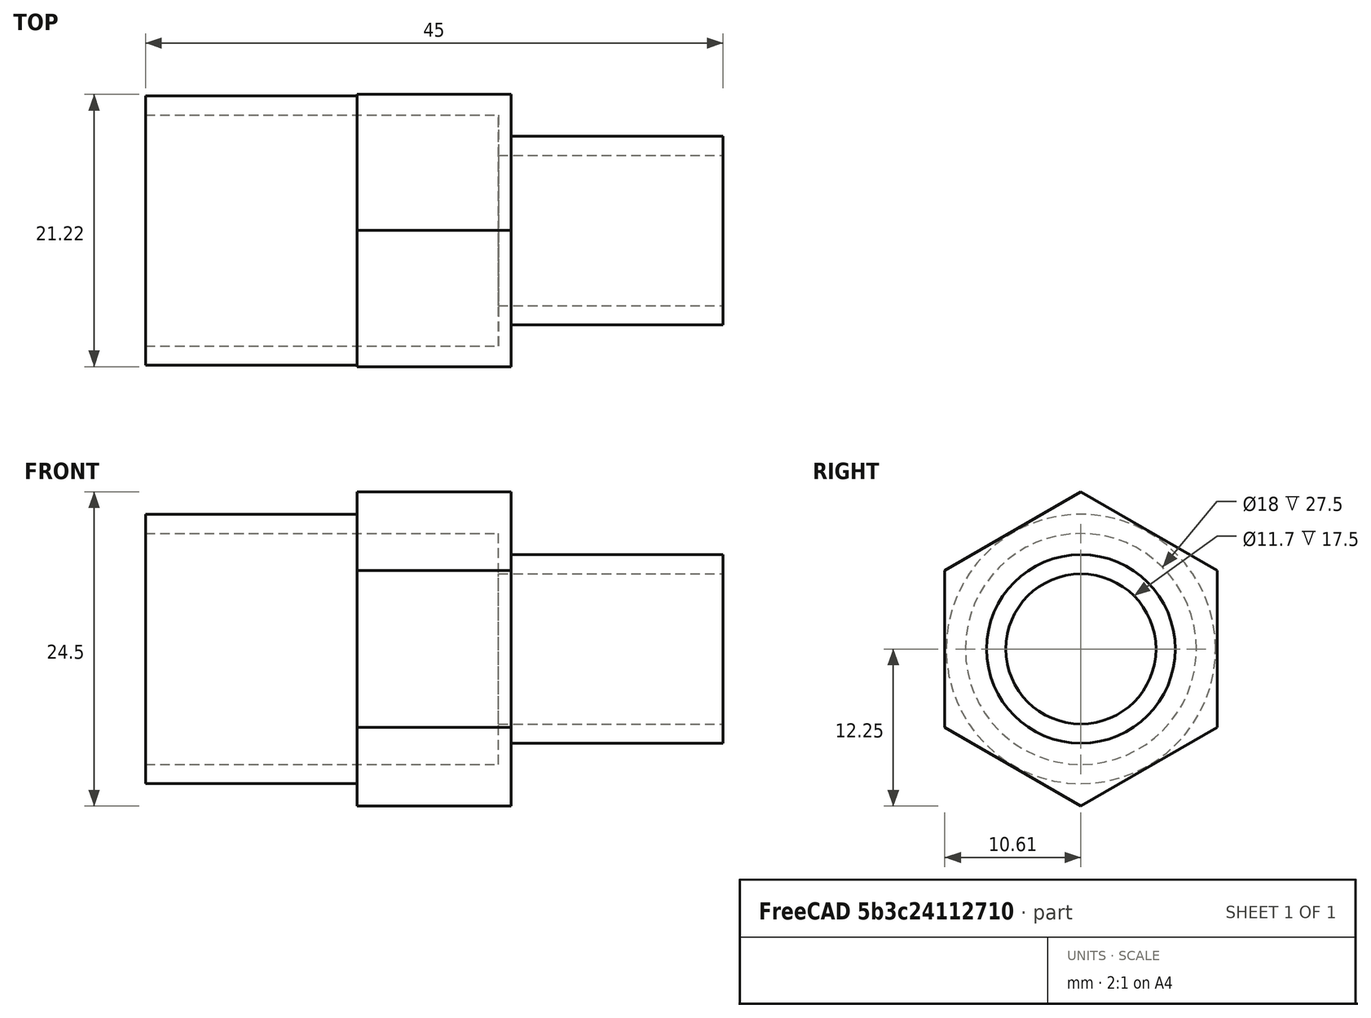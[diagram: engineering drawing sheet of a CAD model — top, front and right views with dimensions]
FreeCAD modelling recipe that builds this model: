
FCSTD DOCUMENT  (FreeCAD 0.16R6706 (Git))
Label: 1_2_to_3_4_NPT_HexNipple
License: All rights reserved
LicenseURL: http://en.wikipedia.org/wiki/All_rights_reserved
objects: Part::Cylinder×4, Part::Part2DObjectPython×1, Part::FeaturePython×1, Part::Extrusion×1, Part::MultiFuse×1, Part::Fuse×1, Part::Cut×1
note: 10 computed .brp shape members not serialized (recipe doc carries the construction recipe); baked Part::Feature solids carry a one-line shape summary decoded from their .brp

FEATURE [Part::Cylinder] cylinder
  Angle = 360
  Height = 25
  Placement = pos=(0,0,-22.5) rot=(0,0,1;0rad)
  Radius = 10.5
FEATURE [Part::Cylinder] cylinder001
  Angle = 360
  Height = 25
  Placement = pos=(0,0,-2.5) rot=(0,0,1;0rad)
  Radius = 7.35
FEATURE [Part::Part2DObjectPython] polygon  # Draft 2D object (typed FeaturePython)
  ChamferSize = 0
  DrawMode = 0
  FacesNumber = 6
  FilletRadius = 0
  MakeFace = true
  Radius = 12.25
FEATURE [Part::FeaturePython] RefineLinearExtrude  # WARN: FeaturePython — macro-defined, semantics opaque (R4)
  Base = -> polygon
FEATURE [Part::Extrusion] LinearExtrude
  Base = -> RefineLinearExtrude
  Dir = (0,0,12)
  Placement = pos=(0,0,-6) rot=(0,0,1;0rad)
  Solid = true
FEATURE [Part::MultiFuse] Group
  Shapes = -> [cylinder,cylinder001,LinearExtrude]
FEATURE [Part::Cylinder] cylinder002
  Angle = 360
  Height = 30
  Placement = pos=(0,0,-25) rot=(0,0,1;0rad)
  Radius = 9
FEATURE [Part::Cylinder] cylinder003
  Angle = 360
  Height = 30
  Placement = pos=(0,0,-5) rot=(0,0,1;0rad)
  Radius = 5.85
FEATURE [Part::Fuse] Group001
  Base = -> cylinder002
  Tool = -> cylinder003
FEATURE [Part::Cut] difference
  Base = -> Group
  Placement = pos=(0,0,0) rot=(0,1,0;1.5708rad)
  Tool = -> Group001
